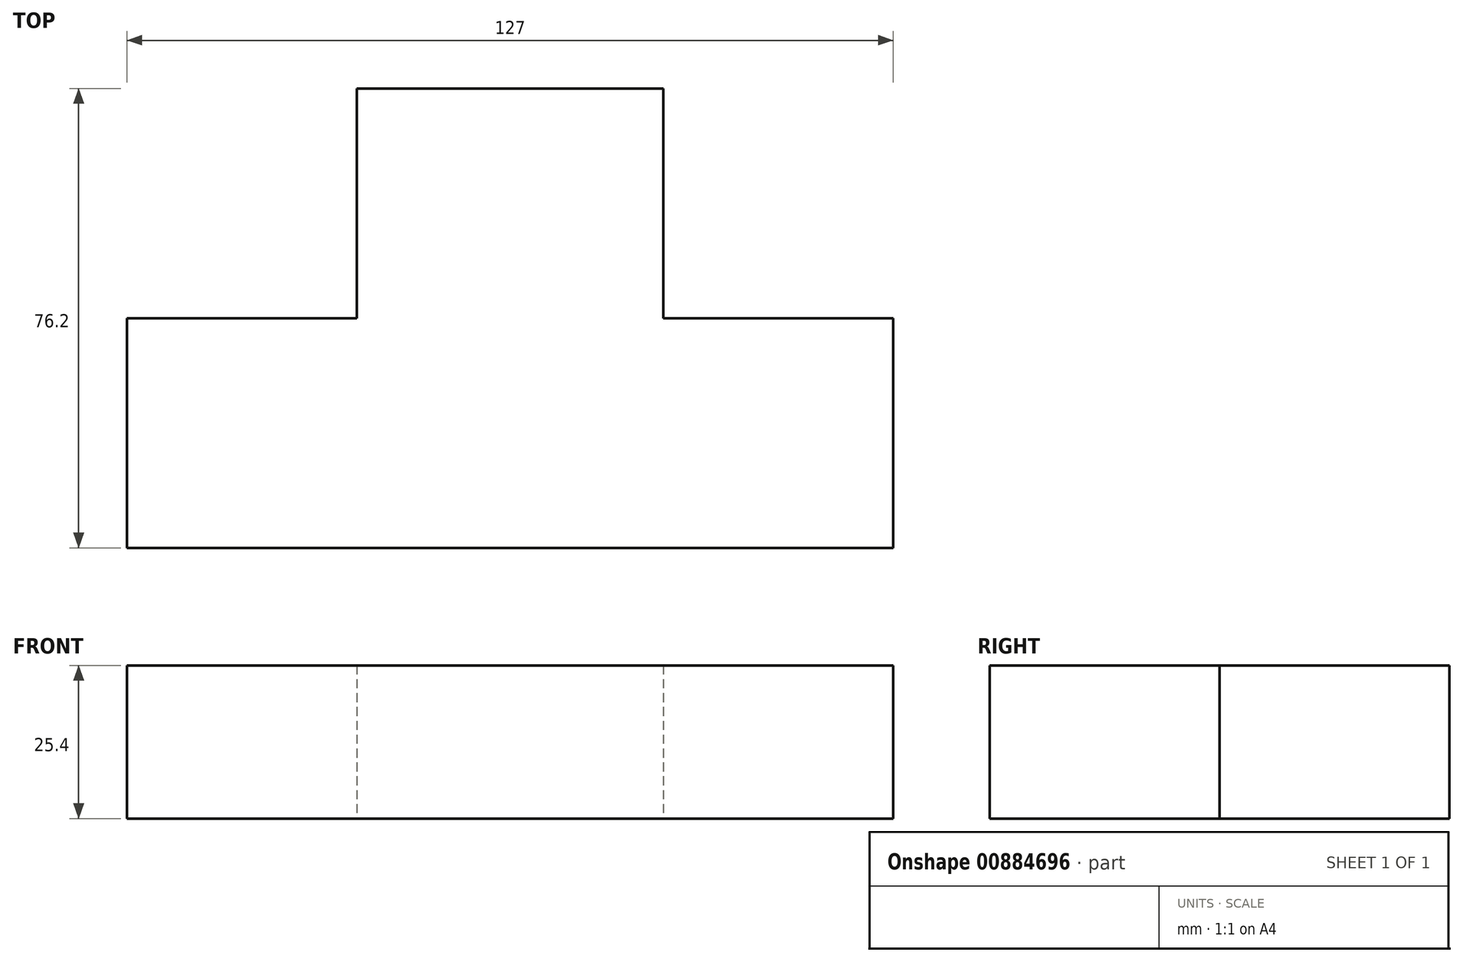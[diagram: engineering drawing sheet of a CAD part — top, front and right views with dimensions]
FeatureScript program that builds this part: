
annotation { "Feature Type Name" : "Feature", "Feature Type Description" : "" }
export const myFeature = defineFeature(function(context is Context, id is Id, definition is map)
    precondition{}
    {
        {
            var Q0;
            Q0=qCreatedBy(makeId("Top.planeOp"),FACE);
            var sketch = newSketch(context, id + "F0", { "sketchPlane" : qUnion([Q0])});
            skLineSegment(sketch, "E0.bottom", {"start": v(63.5, -19.05) * mm, "end": v(-63.5, -19.05) * mm});
            skLineSegment(sketch, "E0.top", {"start": v(63.5, 19.05) * mm, "end": v(25.4, 19.05) * mm});
            skLineSegment(sketch, "E0.left", {"start": v(63.5, -19.05) * mm, "end": v(63.5, 19.05) * mm});
            skLineSegment(sketch, "E0.right", {"start": v(-63.5, -19.05) * mm, "end": v(-63.5, 19.05) * mm});
            skPoint(sketch, "E0.middle", {"position": v(0, 0) * mm});
            skLineSegment(sketch, "E1.bottom", {"start": v(-25.4, 57.15) * mm, "end": v(25.4, 57.15) * mm});
            skLineSegment(sketch, "E1.left", {"start": v(-25.4, 57.15) * mm, "end": v(-25.4, 19.05) * mm});
            skLineSegment(sketch, "E1.right", {"start": v(25.4, 57.15) * mm, "end": v(25.4, 19.05) * mm});
            skPoint(sketch, "E1.top.start.orphan", {"position": v(-25.4, -57.15) * mm});
            skPoint(sketch, "E2.orphan", {"position": v(25.4, -57.15) * mm});
            skLineSegment(sketch, "E3.trimOffspring", {"start": v(-25.4, 19.05) * mm, "end": v(-63.5, 19.05) * mm});
            skLineSegment(sketch, "E4", {"start": v(-25.4, 19.05) * mm, "end": v(25.4, 19.05) * mm});
            skSolve(sketch);
        }
        {
            var Q0;
            Q0 = qSketchRegion(id + "F0", true);
            extrude(context, id + "F1", {"entities" : qUnion([Q0]), "depth" : 25.4 * mm, "offsetDistance" : 25.4 * mm});
        }
    });
